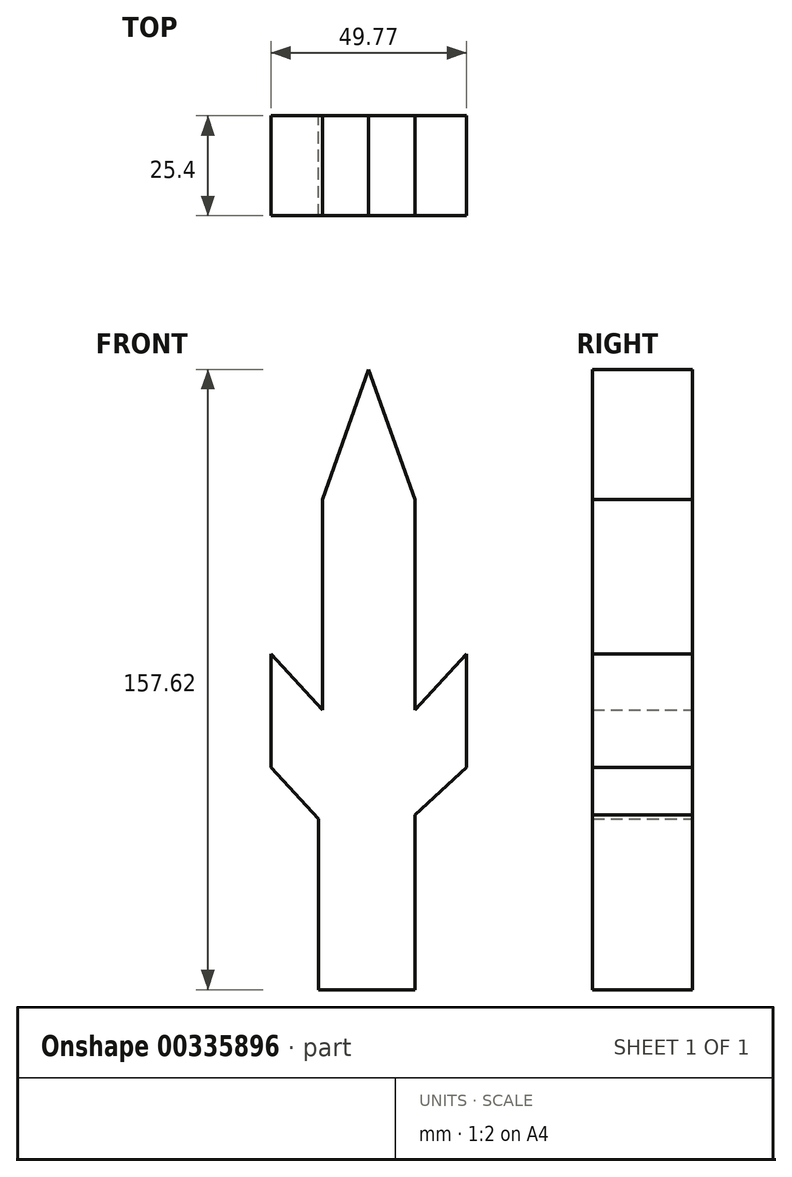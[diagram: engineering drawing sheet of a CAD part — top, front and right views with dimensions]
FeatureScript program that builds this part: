
annotation { "Feature Type Name" : "Feature", "Feature Type Description" : "" }
export const myFeature = defineFeature(function(context is Context, id is Id, definition is map)
    precondition{}
    {
        {
            var Q0;
            Q0=qCreatedBy(makeId("Front.planeOp"),FACE);
            var sketch = newSketch(context, id + "F0", { "sketchPlane" : qUnion([Q0])});
            skLineSegment(sketch, "E0", {"start": v(0, 86.6) * mm, "end": v(-11.78, 53.54) * mm});
            skLineSegment(sketch, "E1", {"start": v(0, 86.6) * mm, "end": v(11.79, 53.54) * mm});
            skLineSegment(sketch, "E2", {"start": v(11.79, 53.54) * mm, "end": v(11.79, 0) * mm});
            skLineSegment(sketch, "E3", {"start": v(-11.78, 53.54) * mm, "end": v(-11.78, 0) * mm});
            skLineSegment(sketch, "E4", {"start": v(11.79, 0) * mm, "end": v(24.9, 14.24) * mm});
            skLineSegment(sketch, "E5", {"start": v(24.9, 14.24) * mm, "end": v(24.9, -14.57) * mm});
            skLineSegment(sketch, "E6", {"start": v(-11.78, 0) * mm, "end": v(-24.88, 14.24) * mm});
            skLineSegment(sketch, "E7", {"start": v(-24.88, 14.24) * mm, "end": v(-24.88, -14.57) * mm});
            skLineSegment(sketch, "E8", {"start": v(24.9, -14.57) * mm, "end": v(11.79, -26.62) * mm});
            skLineSegment(sketch, "E9", {"start": v(-24.88, -14.57) * mm, "end": v(-12.78, -27.63) * mm});
            skLineSegment(sketch, "E10", {"start": v(11.79, -26.62) * mm, "end": v(11.79, -39.42) * mm});
            skLineSegment(sketch, "E11", {"start": v(-12.78, -27.63) * mm, "end": v(-12.78, -39.42) * mm});
            skLineSegment(sketch, "E12", {"start": v(-12.78, -39.42) * mm, "end": v(11.79, -39.42) * mm});
            skSolve(sketch);
        }
        {
            var Q0;
            Q0 = qSketchRegion(id + "FnsrILr0P7dqKnO_0", true);
            var Q1;
            Q1=makeQuery(id+"F0.imprint","IMPRINT",FACE,{"disambiguationData":[TD([[makeQuery(id+"F0.imprint","IMPRINT",EDGE,{"derivedFrom":sQuery(id+"F0.wireOp",EDGE,"E0")}),1.0]])]});
            extrude(context, id + "F1", {"entities" : qUnion([Q0, Q1]), "depth" : 25.4 * mm});
        }
        {
            var Q0;
            Q0=makeQuery(id+"F1.opExtrude","CAP_FACE",FACE,{"disambiguationData":[OSD([sQuery(id+"F0.wireOp",EDGE,"E0"),sQuery(id+"F0.wireOp",EDGE,"E1"),sQuery(id+"F0.wireOp",EDGE,"E2"),sQuery(id+"F0.wireOp",EDGE,"E3"),sQuery(id+"F0.wireOp",EDGE,"E4"),sQuery(id+"F0.wireOp",EDGE,"E5"),sQuery(id+"F0.wireOp",EDGE,"E6"),sQuery(id+"F0.wireOp",EDGE,"E7"),sQuery(id+"F0.wireOp",EDGE,"E8"),sQuery(id+"F0.wireOp",EDGE,"E9"),sQuery(id+"F0.wireOp",EDGE,"E10"),sQuery(id+"F0.wireOp",EDGE,"E11"),sQuery(id+"F0.wireOp",EDGE,"E12")])],"isStart":false});
            var sketch = newSketch(context, id + "F2", { "sketchPlane" : qUnion([Q0])});
            skLineSegment(sketch, "E13", {"start": v(-12.78, -39.42) * mm, "end": v(-12.78, -71.01) * mm});
            skLineSegment(sketch, "E14", {"start": v(11.79, -39.42) * mm, "end": v(11.79, -71.01) * mm});
            skLineSegment(sketch, "E15", {"start": v(-12.78, -71.01) * mm, "end": v(11.79, -71.01) * mm});
            skLineSegment(sketch, "E16", {"start": v(11.79, -71.01) * mm, "end": v(-12.78, -55.2) * mm});
            skLineSegment(sketch, "E17", {"start": v(-12.78, -39.42) * mm, "end": v(11.79, -55.21) * mm});
            skLineSegment(sketch, "E18", {"start": v(-12.78, -71.01) * mm, "end": v(11.79, -55.21) * mm});
            skLineSegment(sketch, "E19", {"start": v(-12.78, -55.2) * mm, "end": v(11.79, -39.42) * mm});
            skSolve(sketch);
        }
        {
            var Q0;
            {var subQ1=sQuery(id+"F2.wireOp",EDGE,"E16");var subQ3=sQuery(id+"F2.wireOp",EDGE,"E18");var subQ4=makeQuery(id+"F2.imprint","INTERSECT",VERTEX,{"derivedFrom":[subQ1,subQ3]});Q0=makeQuery(id+"F2.imprint","IMPRINT",FACE,{"disambiguationData":[TD([[makeQuery(id+"F2.imprint","IMPRINT",EDGE,{"disambiguationData":[TD([[subQ4,-1.0]])],"derivedFrom":subQ1}),-1.0]])]});}
            var Q1;
            {var subQ1=makeQuery(id+"F1.opExtrude","CAP_EDGE",EDGE,{"disambiguationData":[OSD([sQuery(id+"F0.wireOp",EDGE,"E12")])],"isStart":false});Q1=makeQuery(id+"F2.imprint","IMPRINT",FACE,{"disambiguationData":[TD([[makeQuery(id+"F2.imprint","IMPRINT",EDGE,{"derivedFrom":subQ1}),-1.0]])]});}
            var Q2;
            {var subQ0=sQuery(id+"F2.wireOp",EDGE,"E15");Q2=makeQuery(id+"F2.imprint","IMPRINT",FACE,{"disambiguationData":[TD([[makeQuery(id+"F2.imprint","IMPRINT",EDGE,{"derivedFrom":subQ0}),1.0]])]});}
            var Q3;
            {var subQ0=sQuery(id+"F2.wireOp",EDGE,"E19");var subQ3=sQuery(id+"F2.wireOp",EDGE,"E17");var subQ5=makeQuery(id+"F2.imprint","INTERSECT",VERTEX,{"derivedFrom":[subQ3,subQ0]});Q3=makeQuery(id+"F2.imprint","IMPRINT",FACE,{"disambiguationData":[TD([[makeQuery(id+"F2.imprint","IMPRINT",EDGE,{"disambiguationData":[TD([[subQ5,-1.0]])],"derivedFrom":subQ3}),1.0]])]});}
            var Q4;
            {var subQ0=sQuery(id+"F2.wireOp",EDGE,"E17");var subQ3=sQuery(id+"F2.wireOp",EDGE,"E19");var subQ5=makeQuery(id+"F2.imprint","INTERSECT",VERTEX,{"derivedFrom":[subQ0,subQ3]});Q4=makeQuery(id+"F2.imprint","IMPRINT",FACE,{"disambiguationData":[TD([[makeQuery(id+"F2.imprint","IMPRINT",EDGE,{"disambiguationData":[TD([[subQ5,1.0]])],"derivedFrom":subQ3}),1.0]])]});}
            var Q5;
            {var subQ0=sQuery(id+"F2.wireOp",EDGE,"E16");var subQ3=sQuery(id+"F2.wireOp",EDGE,"E18");var subQ5=makeQuery(id+"F2.imprint","INTERSECT",VERTEX,{"derivedFrom":[subQ0,subQ3]});Q5=makeQuery(id+"F2.imprint","IMPRINT",FACE,{"disambiguationData":[TD([[makeQuery(id+"F2.imprint","IMPRINT",EDGE,{"disambiguationData":[TD([[subQ5,1.0]])],"derivedFrom":subQ0}),-1.0]])]});}
            var Q6;
            {var subQ0=sQuery(id+"F2.wireOp",EDGE,"E18");var subQ3=sQuery(id+"F2.wireOp",EDGE,"E16");var subQ5=makeQuery(id+"F2.imprint","INTERSECT",VERTEX,{"derivedFrom":[subQ3,subQ0]});Q6=makeQuery(id+"F2.imprint","IMPRINT",FACE,{"disambiguationData":[TD([[makeQuery(id+"F2.imprint","IMPRINT",EDGE,{"disambiguationData":[TD([[subQ5,-1.0]])],"derivedFrom":subQ3}),1.0]])]});}
            extrude(context, id + "F3", {"entities" : qUnion([Q0, Q1, Q2, Q3, Q4, Q5, Q6]), "operationType" : NewBodyOperationType.ADD, "oppositeDirection" : true, "depth" : 25.4 * mm});
        }
    });
